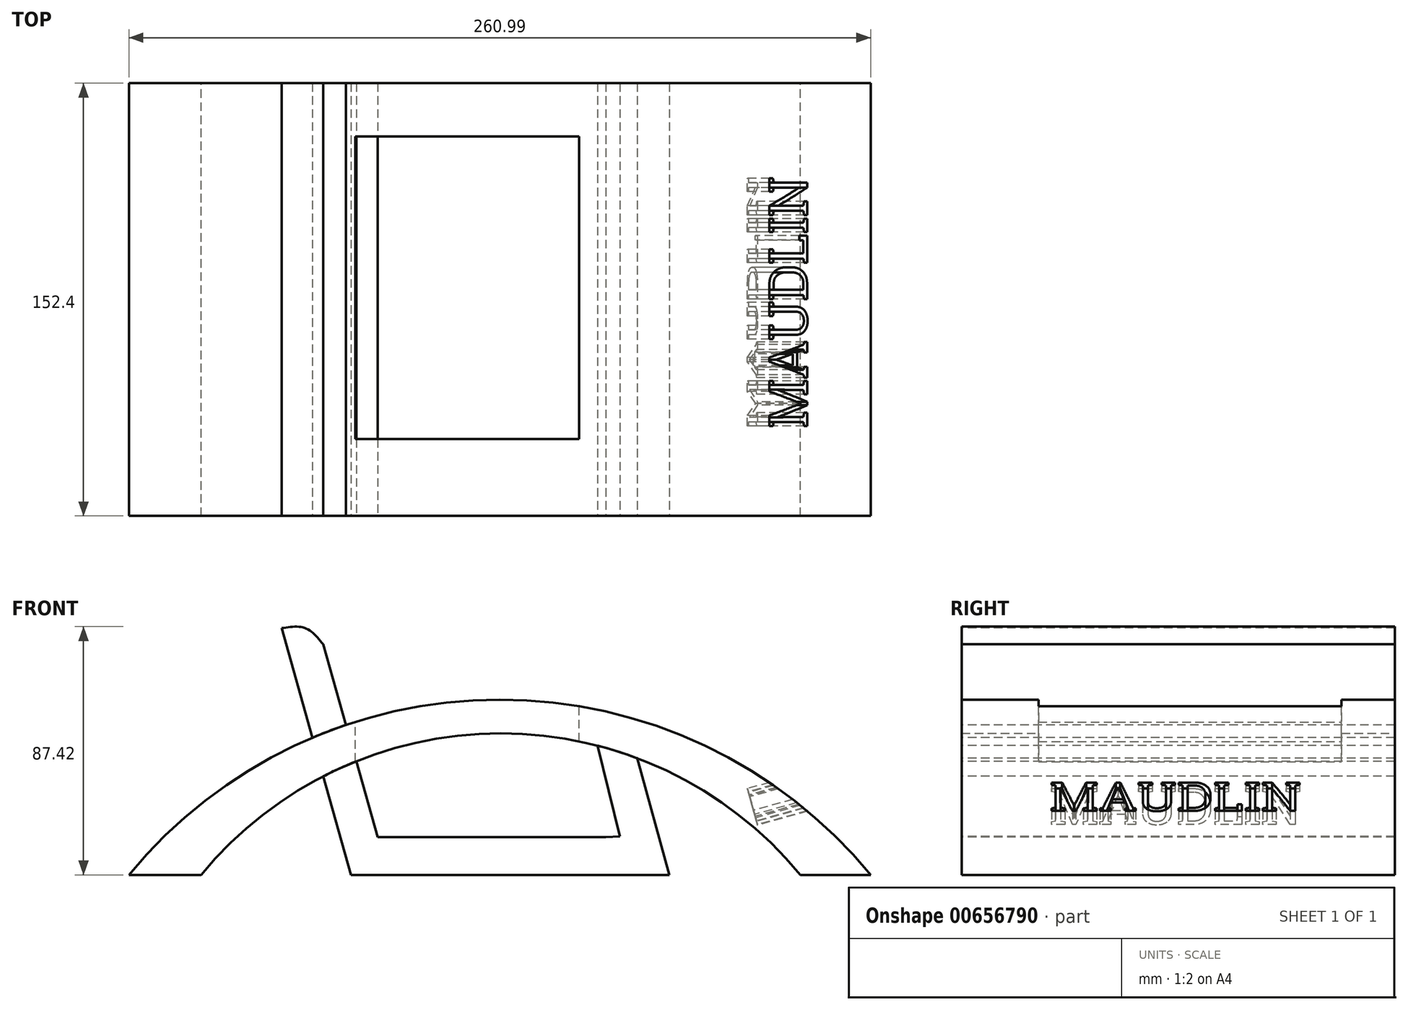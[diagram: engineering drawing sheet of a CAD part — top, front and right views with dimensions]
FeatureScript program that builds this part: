
annotation { "Feature Type Name" : "Feature", "Feature Type Description" : "" }
export const myFeature = defineFeature(function(context is Context, id is Id, definition is map)
    precondition{}
    {
        {
            var Q0;
            Q0=qCreatedBy(makeId("Front.planeOp"),FACE);
            var sketch = newSketch(context, id + "F0", { "sketchPlane" : qUnion([Q0])});
            skArc(sketch, "E0", {"start": v(92.46, 0) * mm, "mid": v(-12.95, 49.8) * mm, "end": v(-118.36, 0) * mm});
            skArc(sketch, "E1", {"start": v(117.23, 0) * mm, "mid": v(-13.27, 61.7) * mm, "end": v(-143.76, 0) * mm});
            skLineSegment(sketch, "E2", {"start": v(92.46, 0) * mm, "end": v(117.23, 0) * mm});
            skFitSpline(sketch, "E3", {"points": [v(-40.83, 46.62) * mm, v(-41.87, 46.7) * mm], "startDerivative": vector(-1.04, 0.1) * mm, "endDerivative": vector(-1.04, 0.1) * mm});
            skFitSpline(sketch, "E4", {"points": [v(-47.76, 44.77) * mm, v(-48.24, 45.16) * mm], "startDerivative": vector(-0.48, 0.4) * mm, "endDerivative": vector(-0.48, 0.4) * mm});
            skLineSegment(sketch, "E5", {"start": v(-143.76, 0) * mm, "end": v(-118.36, 0) * mm});
            skFitSpline(sketch, "E6", {"points": [v(-48, 44.48) * mm, v(-47.76, 44.77) * mm], "startDerivative": vector(0.25, 0.29) * mm, "endDerivative": vector(0.25, 0.29) * mm});
            skSolve(sketch);
        }
        {
            var Q0;
            {var subQ0=sQuery(id+"F0.wireOp",EDGE,"E5");Q0=makeQuery(id+"F0.imprint","IMPRINT",FACE,{"disambiguationData":[TD([[makeQuery(id+"F0.imprint","IMPRINT",EDGE,{"derivedFrom":subQ0}),1.0]])]});}
            var Q1;
            {var subQ5=sQuery(id+"F0.wireOp",EDGE,"117a304a-8356-408d-b649-f69c5db0d157");Q1=makeQuery(id+"F0.imprint","IMPRINT",FACE,{"disambiguationData":[TD([[makeQuery(id+"F0.imprint","IMPRINT",EDGE,{"derivedFrom":subQ5}),-1.0]])]});}
            var Q2;
            {var subQ6=sQuery(id+"F0.wireOp",EDGE,"E2");Q2=makeQuery(id+"F0.imprint","IMPRINT",FACE,{"disambiguationData":[TD([[makeQuery(id+"F0.imprint","IMPRINT",EDGE,{"derivedFrom":subQ6}),1.0]])]});}
            var Q3;
            {var subQ3=sQuery(id+"F0.wireOp",EDGE,"E1");var subQ5=sQuery(id+"F0.wireOp",EDGE,"5f8b165e-f229-4f9b-8518-06e8f09e9d1f");var subQ6=makeQuery(id+"F0.imprint","INTERSECT",VERTEX,{"derivedFrom":[subQ3,subQ5]});Q3=makeQuery(id+"F0.imprint","IMPRINT",FACE,{"disambiguationData":[TD([[makeQuery(id+"F0.imprint","IMPRINT",EDGE,{"disambiguationData":[TD([[subQ6,-1.0]])],"derivedFrom":subQ3}),1.0]])]});}
            var Q4;
            {var subQ0=sQuery(id+"F0.wireOp",EDGE,"oG4XOCTQ-GZYg-zBtZ-jh42-P3STFEbOaWm5");Q4=makeQuery(id+"F0.imprint","IMPRINT",FACE,{"disambiguationData":[TD([[makeQuery(id+"F0.imprint","IMPRINT",EDGE,{"derivedFrom":subQ0}),1.0]])]});}
            extrude(context, id + "F1", {"entities" : qUnion([Q0, Q1, Q2, Q3, Q4]), "depth" : 152.4 * mm, "offsetDistance" : 25.4 * mm});
        }
        {
            var Q0;
            Q0=qCreatedBy(makeId("Top.planeOp"),FACE);
            var sketch = newSketch(context, id + "F2", { "sketchPlane" : qUnion([Q0])});
            skLineSegment(sketch, "E7.bottom", {"start": v(-64.14, -18.77) * mm, "end": v(14.6, -18.77) * mm});
            skLineSegment(sketch, "E7.top", {"start": v(-64.14, -125.35) * mm, "end": v(14.6, -125.35) * mm});
            skLineSegment(sketch, "E7.left", {"start": v(-64.14, -18.77) * mm, "end": v(-64.14, -125.35) * mm});
            skLineSegment(sketch, "E7.right", {"start": v(14.6, -18.77) * mm, "end": v(14.6, -125.35) * mm});
            skSolve(sketch);
        }
        {
            var Q0;
            Q0 = qSketchRegion(id + "F2", true);
            extrude(context, id + "F3", {"entities" : qUnion([Q0]), "operationType" : NewBodyOperationType.REMOVE, "oppositeDirection" : true, "depth" : 27.94 * mm, "offsetDistance" : 25.4 * mm, "hasSecondDirection" : true, "secondDirectionOppositeDirection" : false, "secondDirectionDepth" : 119.38 * mm});
        }
        {
            var Q0;
            Q0=makeQuery(id+"F1.opExtrude","CAP_FACE",FACE,{"disambiguationData":[OSD([sQuery(id+"F0.wireOp",EDGE,"E0"),sQuery(id+"F0.wireOp",EDGE,"E1"),sQuery(id+"F0.wireOp",EDGE,"E5"),sQuery(id+"F0.wireOp",EDGE,"E2")])],"isStart":false});
            var sketch = newSketch(context, id + "F4", { "sketchPlane" : qUnion([Q0])});
            skLineSegment(sketch, "E8", {"start": v(35.08, 41.07) * mm, "end": v(46.45, 0) * mm});
            skLineSegment(sketch, "E9", {"start": v(24.07, 13.3) * mm, "end": v(-43.58, 13.3) * mm});
            skLineSegment(sketch, "E10", {"start": v(-75.39, 81.18) * mm, "end": v(-56.19, 13.3) * mm});
            skLineSegment(sketch, "E11", {"start": v(-43.58, 13.3) * mm, "end": v(-56.19, 13.3) * mm});
            skLineSegment(sketch, "E12", {"start": v(-65.65, 0) * mm, "end": v(46.45, 0) * mm});
            skLineSegment(sketch, "E13", {"start": v(-65.65, 0) * mm, "end": v(-89.97, 86.88) * mm});
            skLineSegment(sketch, "E14", {"start": v(21.09, 45.5) * mm, "end": v(28.93, 13.5) * mm});
            skLineSegment(sketch, "E15", {"start": v(24.07, 13.3) * mm, "end": v(28.93, 13.5) * mm});
            skFitSpline(sketch, "E16", {"points": [v(-89.97, 86.88) * mm, v(-81.65, 86.88) * mm, v(-75.39, 81.18) * mm], "startDerivative": vector(17.77, 2.83) * mm, "endDerivative": vector(11.4, -14.2) * mm});
            skSolve(sketch);
        }
        {
            var Q0;
            {var subQ4=sQuery(id+"F4.wireOp",EDGE,"E8");Q0=makeQuery(id+"F4.imprint","IMPRINT",FACE,{"disambiguationData":[TD([[makeQuery(id+"F4.imprint","IMPRINT",EDGE,{"derivedFrom":subQ4}),-1.0]])]});}
            var Q1;
            {var subQ0=sQuery(id+"F4.wireOp",EDGE,"E16");Q1=makeQuery(id+"F4.imprint","IMPRINT",FACE,{"disambiguationData":[TD([[makeQuery(id+"F4.imprint","IMPRINT",EDGE,{"derivedFrom":subQ0}),-1.0]])]});}
            extrude(context, id + "F5", {"entities" : qUnion([Q0, Q1]), "oppositeDirection" : true, "depth" : 152.4 * mm, "offsetDistance" : 25.4 * mm});
        }
        {
            var Q0;
            Q0=makeQuery(id+"F5.opExtrude","SWEPT_FACE",FACE,{"disambiguationData":[OSD([sQuery(id+"F4.wireOp",EDGE,"E8")])]});
            var sketch = newSketch(context, id + "F6", { "sketchPlane" : qUnion([Q0])});
            skText(sketch, "E17", { "text": "MAUDLIN", "fontName": "RobotoSlab-Regular.ttf"});
            skFitSpline(sketch, "E18", {"points": [v(-72.58, 15.7) * mm, v(-72.58, 15.77) * mm, v(-72.6, 15.87) * mm], "startDerivative": vector(0.01, 0.15) * mm, "endDerivative": vector(-0.06, 0.19) * mm});
            skLineSegment(sketch, "E19.right", {"start": v(-22.56, -2.96) * mm, "end": v(-22.56, -3.59) * mm});
            const initialGuessF6  = {"E17": [-0.12142, -0.00359, 1, 0, 0.01333]};
            skSetInitialGuess(sketch, initialGuessF6);
            skSolve(sketch);
        }
        {
            var Q0;
            Q0 = qSketchRegion(id + "F6", true);
            extrude(context, id + "F7", {"entities" : qUnion([Q0]), "operationType" : NewBodyOperationType.REMOVE, "depth" : 58.42 * mm, "offsetDistance" : 25.4 * mm, "hasSecondDirection" : true, "secondDirectionOppositeDirection" : false, "secondDirectionDepth" : 34.54 * mm});
        }
    });
